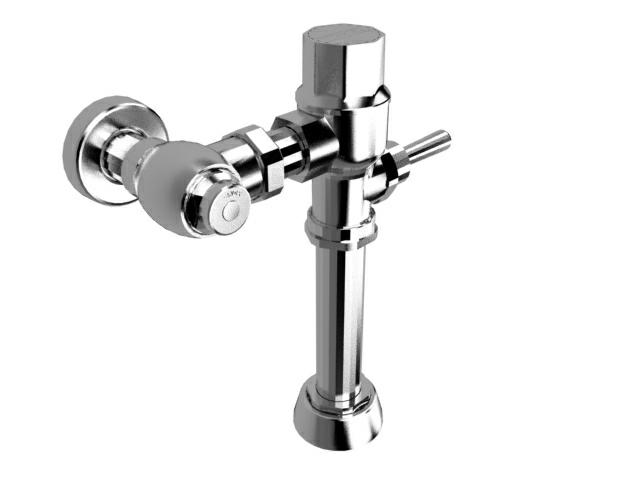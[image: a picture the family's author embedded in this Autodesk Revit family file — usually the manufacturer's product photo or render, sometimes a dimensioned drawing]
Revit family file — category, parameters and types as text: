
# Revit family: 110-WC-4.8_RFA
name_source: partatom
category: Modelos genéricos
units: mm (PartAtom-declared; Revit-internal decimal feet)

## family parameters
Anfitrión = Cara
Compartido = Sí
Corte con vacíos al cargar = No
Cota de conector redondo = Diámetro de uso
Número OmniClass = 23.45.05.14.99
Puede alojar armadura = No
Punto de cálculo de habitación = Sí
Tipo de pieza = Normal
Título OmniClass = Other Sanitary Washing Plumbing Fixtures

## types (1)
- 110-WC-4.8
    Comentarios de tipo = Fluxómetro para W. C. de manija
    Compliance = NOM-005-CONAGUA-1996
    Connection = 1"
    Descripción = Fluxómetro para W. C. de manija con recubrimiento antibacterial. Entrada superior para spud de 32 mm ó 38 mm. Descarga de 4,8 l por accionamiento. Camisa recortable. Conexión izquierda o derecha. Niple recto Ø 32 mm x 9" de largo
    Elevación por defecto = 17 "
    Fabricante = HELVEX S.A. DE C.V.
    Imagen de tipo = 110-WC-4.8.jpg
    Material = Brass Chromed
    Max. Working Pressure = 85.3 psi
    Min. Working Pressure = 14.2 psi
    Modelo = 110-WC-4.8
    Note = La tubería de alimentación debe tener un Ø 32 mm mínimo y debe conectarse una reducción de campana de 32 mm - 25 mm a la llave de retención.
    URL = http://www.helvex.com.mx

## geometry (parser evidence)
native form markers: Sweep x4
no freeform markers — native parametric forms only
